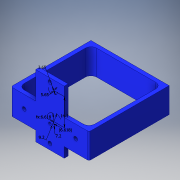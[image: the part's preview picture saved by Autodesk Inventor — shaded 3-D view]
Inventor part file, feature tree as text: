
AUTODESK INVENTOR PART (.ipt)
format: ipt  version: 2016 (Build 200138000, 138)  size: 310,272 bytes
history: native  units: in
note: dims shown in document units (in); Inventor stores cm internally (conversion verified against a paired STEP export)
features: sketch x8, extrude x6, fillet x6, hole x2
ambient origin geometry x8: Origin, YZ Plane, XZ Plane, XY Plane, X Axis, Y Axis, Z Axis, Center Point
bodies: Solid1 (feature_tree)
feature tree (22):
  extrude  "Extrusion1"  Depth=0.5197in
  extrude  "Extrusion10"  Depth=0.0787in
  extrude  "Extrusion11"  Depth=0.2096in TaperAngle=0.0deg
  hole  "Hole2"  [1 undecoded]
  extrude  "Extrusion12"  Depth=0.2953in
  fillet  "Fillet17"  Radius=0.2953in
  hole  "Hole3"  [1 undecoded]
  fillet  "Fillet19"  Radius=0.2756in
  fillet  "Fillet20"  Radius=0.0787in
  extrude  "Extrusion13"  Depth=0.1181in
  fillet  "Fillet21"  Radius=0.1181in
  fillet  "Fillet22"  Radius=0.2598in
  extrude  "Extrusion14"  Depth=0.1181in
  fillet  "Fillet23"  Radius=0.1181in
  sketch  "Sketch1"  dims[d0=1.6142in d1=0.5197in]
  sketch  "Sketch15"  dims[d2=0.0787in d3=0.0in d79=0.5118in]
  sketch  "Sketch16"  dims[d80=0.5118in d81=0.2096in d82=0.0in]
  sketch  "Sketch17"  dims[d83=0.5118in d84=0.5118in]
  sketch  "Sketch19"  dims[d85=0.562in d86=0.0in d87=0.2953in d88=0.2953in]
  sketch  "Sketch20"  dims[d89=0.2598in d90=0.2598in d91=0.2756in d92=0.0787in]
  sketch  "Sketch22"  dims[d93=0.2953in d94=0.2953in d95=0.1181in d96=0.2598in]
  sketch  "Sketch23"  dims[d97=0.2598in d98=0.2756in d99=0.0787in d100=0.2362in d101=0.1575in d102=0.0787in d103=90.0deg d104=0.1181in d105=0.8108in d108=0.2835in d110=0.2605in d111=0.2605in d112=0.3622in d113=0.1437in d114=0.5551in d115=0.2224in d116=0.0787in d120=0.1181in d121=0.0in d122=0.1181in d124=0.0591in d125=0.2362in d126=0.1575in d127=0.0787in d128=90.0deg d129=0.315in d130=0.8108in d131=0.1142in d132=0.0394in d133=0.0787in d134=0.0787in d135=1.5748in d136=0.0in d137=0.1181in d138=0.0394in d139=0.0787in d140=1.5748in d141=1.4567in d142=0.0in d143=0.1181in]
note: 2 required parameter values undecoded (feature->parameter linkage not recoverable at this tier; creation-order binding heuristic only, values carry confidence <= 0.55)
